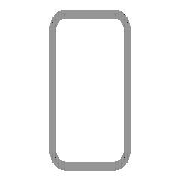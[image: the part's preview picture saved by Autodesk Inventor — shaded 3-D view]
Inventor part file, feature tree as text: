
AUTODESK INVENTOR PART (.ipt)
format: ipt  version: 2025 (Build 290162010, 162A)  size: 130,560 bytes
history: native  units: mm (DEFAULTED — no unit token found)
features: other x3, sketch x1, plane x1
ambient origin geometry x8: Origin, YZ Plane, XZ Plane, XY Plane, X Axis, Y Axis, Z Axis, Center Point
bodies: Solid1 (feature_tree), Body (feature_tree)
feature tree (5):
  other  "Driven Length"
  other  "Start plane"
  other  "End plane"
  sketch  "Sketch3"  dims[d3=2925.0mm d4=0.0mm d7=6.0mm d10=120.0mm d11=80.0mm d12=3.0mm d13=-0.0mm d14=2925.0mm d15=60.0mm d16=40.0mm d17=90.0deg d18=2925.0mm]
  plane  "Work Plane3"
